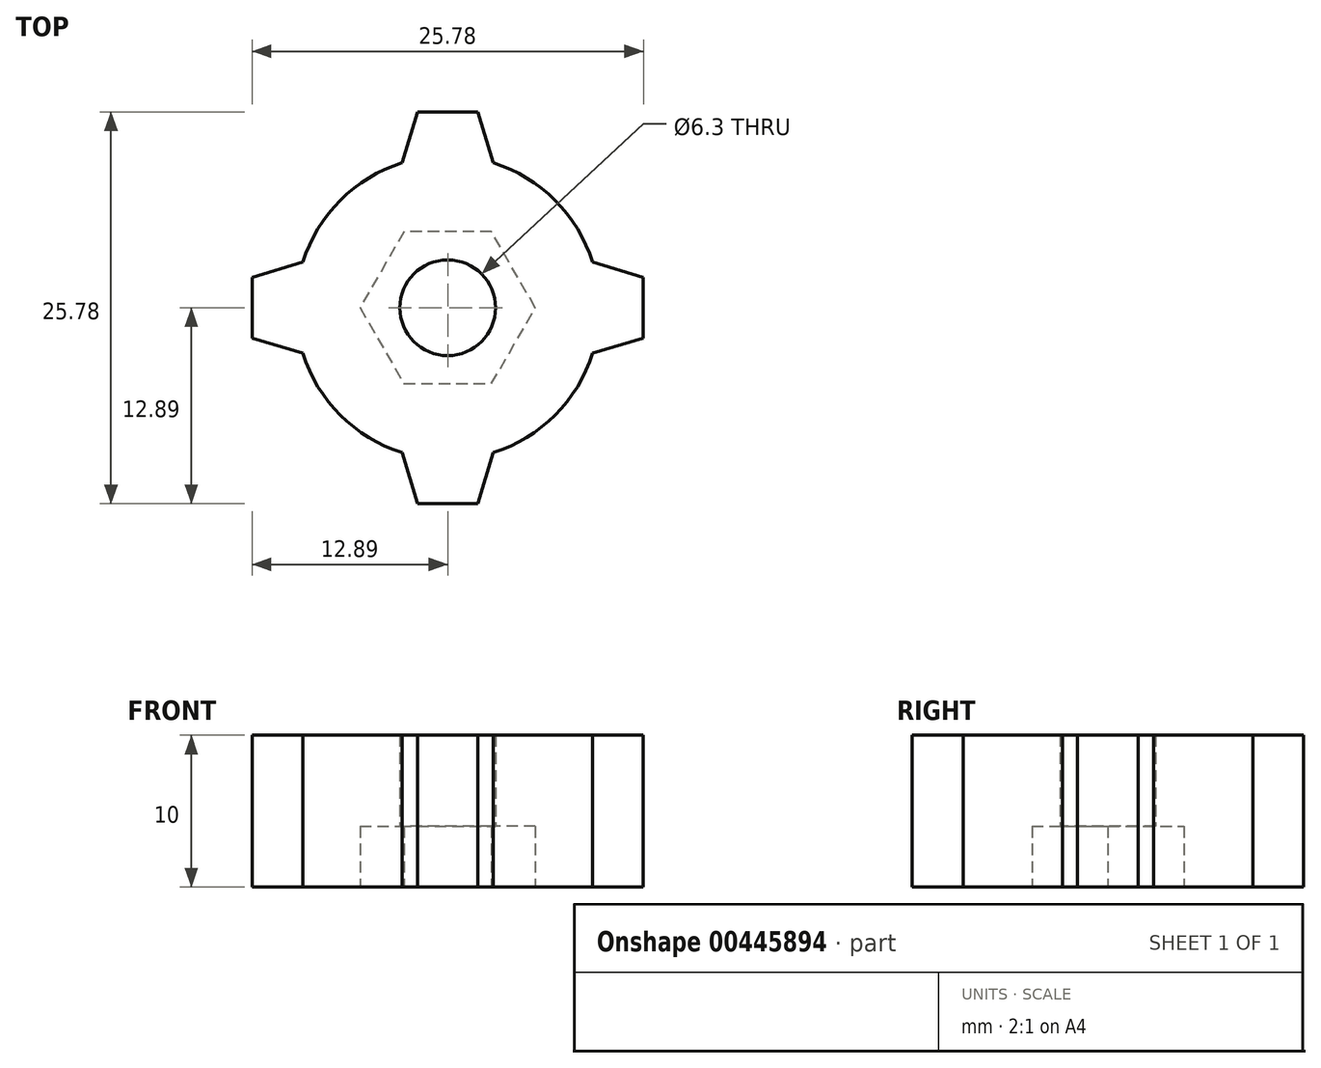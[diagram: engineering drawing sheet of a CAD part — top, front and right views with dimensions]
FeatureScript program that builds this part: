
annotation { "Feature Type Name" : "Feature", "Feature Type Description" : "" }
export const myFeature = defineFeature(function(context is Context, id is Id, definition is map)
    precondition{}
    {
        {
            var Q0;
            Q0=qCreatedBy(makeId("Top.planeOp"),FACE);
            var sketch = newSketch(context, id + "F0", { "sketchPlane" : qUnion([Q0])});
            skCircle(sketch, "E0", {"center": v(0, 0) * mm, "radius": 10 * mm});
            skPoint(sketch, "E1", {"position": v(0, -10) * mm});
            skLineSegment(sketch, "E2", {"start": v(-3, -9.54) * mm, "end": v(-2, -12.89) * mm});
            skLineSegment(sketch, "E3", {"start": v(-2, -12.89) * mm, "end": v(0, -12.89) * mm});
            skLineSegment(sketch, "E4", {"start": v(0, -12.89) * mm, "end": v(0, -10) * mm, "construction": true});
            skLineSegment(sketch, "E5.MirrorCS", {"start": v(2, -12.89) * mm, "end": v(0, -12.89) * mm});
            skLineSegment(sketch, "E6.MirrorCS", {"start": v(3, -9.54) * mm, "end": v(2, -12.89) * mm});
            skSolve(sketch);
        }
        {
            var Q0;
            Q0=makeQuery(id+"F0.imprint","IMPRINT",FACE,{"disambiguationData":[TD([[makeQuery(id+"F0.imprint","IMPRINT",EDGE,{"derivedFrom":sQuery(id+"F0.wireOp",EDGE,"E0")}),1.0]])]});
            extrude(context, id + "F1", {"entities" : qUnion([Q0]), "depth" : 10 * mm});
        }
        {
            var Q0;
            Q0=makeQuery(id+"F1.opExtrude","CAP_FACE",FACE,{"disambiguationData":[OSD([sQuery(id+"F0.wireOp",EDGE,"E0")])],"isStart":true});
            var sketch = newSketch(context, id + "F2", { "sketchPlane" : qUnion([Q0])});
            skCircle(sketch, "E7.cCircle", {"center": v(0, 0) * mm, "radius": 5 * mm, "construction": true});
            skLineSegment(sketch, "E7.0", {"start": v(2.89, -5) * mm, "end": v(-2.89, -5) * mm});
            skLineSegment(sketch, "E7.1", {"start": v(-2.89, -5) * mm, "end": v(-5.77, 0) * mm});
            skLineSegment(sketch, "E7.2", {"start": v(-5.77, 0) * mm, "end": v(-2.89, 5) * mm});
            skLineSegment(sketch, "E7.3", {"start": v(-2.89, 5) * mm, "end": v(2.89, 5) * mm});
            skLineSegment(sketch, "E7.4", {"start": v(2.89, 5) * mm, "end": v(5.77, 0) * mm});
            skLineSegment(sketch, "E7.5", {"start": v(5.77, 0) * mm, "end": v(2.89, -5) * mm});
            skPoint(sketch, "E7.0.midPoint", {"position": v(0, -5) * mm});
            skSolve(sketch);
        }
        {
            var Q0;
            Q0=makeQuery(id+"F2.imprint","IMPRINT",FACE,{"disambiguationData":[TD([[makeQuery(id+"F2.imprint","IMPRINT",EDGE,{"derivedFrom":sQuery(id+"F2.wireOp",EDGE,"E7.0")}),-1.0]])]});
            extrude(context, id + "F3", {"entities" : qUnion([Q0]), "operationType" : NewBodyOperationType.REMOVE, "oppositeDirection" : true, "depth" : 4 * mm});
        }
        {
            var Q0;
            Q0=sQuery(id+"F2.wireOp",VERTEX,"E7.cCircle.center");
            var Q1;
            Q1=makeQuery(id+"F1.opExtrude","SWEPT_BODY",BODY,{"disambiguationData":[OSD([sQuery(id+"F0.wireOp",EDGE,"E0")])]});
            hole(context, id + "F4", {"style" : HoleStyle.SIMPLE, "endStyle" : HoleEndStyle.THROUGH, "standardTappedOrClearance" : lookupTablePath({ "standard" : "ISO", "fit" : "Close", "size" : "M6", "type" : "Clearance" }), "standardBlindInLast" : lookupTablePath({ "fit" : "Close", "standard" : "ISO", "size" : "M6", "type" : "Clearance" }), "holeDiameter" : 6.3 * mm, "isTappedThrough" : true, "tappedDepth" : 12 * mm, "tapClearance" : 3, "locations" : qUnion([Q0]), "scope" : qUnion([Q1])});
        }
        {
            var Q0;
            {var subQ0=sQuery(id+"F0.wireOp",EDGE,"E2");Q0=makeQuery(id+"F0.imprint","IMPRINT",FACE,{"disambiguationData":[TD([[makeQuery(id+"F0.imprint","IMPRINT",EDGE,{"derivedFrom":subQ0}),1.0]])]});}
            var Q1;
            Q1=makeQuery(id+"F1.opExtrude","CAP_FACE",FACE,{"disambiguationData":[OSD([sQuery(id+"F0.wireOp",EDGE,"E0")])],"isStart":false});
            extrude(context, id + "F5", {"entities" : qUnion([Q0]), "endBound" : BoundingType.UP_TO_SURFACE, "endBoundEntityFace" : qUnion([Q1]), "depth" : 25 * mm});
        }
        {
            var Q0;
            Q0=qCreatedBy(makeId("Front.planeOp"),FACE);
            var sketch = newSketch(context, id + "F6", { "sketchPlane" : qUnion([Q0])});
            skLineSegment(sketch, "E8", {"start": v(0, 0) * mm, "end": v(0, -24.05) * mm});
            skSolve(sketch);
        }
        {
            var Q0;
            Q0=makeQuery(id+"F5.opExtrude","SWEPT_BODY",BODY,{"disambiguationData":[OSD([sQuery(id+"F0.wireOp",EDGE,"E0"),sQuery(id+"F0.wireOp",EDGE,"E2"),sQuery(id+"F0.wireOp",EDGE,"E3"),sQuery(id+"F0.wireOp",EDGE,"E5.MirrorCS"),sQuery(id+"F0.wireOp",EDGE,"E6.MirrorCS")])]});
            var Q1;
            Q1=sQuery(id+"F6.wireOp",EDGE,"E8");
            circularPattern(context, id + "F7", {"operationType" : NewBodyOperationType.ADD, "entities" : qUnion([Q0]), "axis" : qUnion([Q1]), "angle" : 360 * degree, "instanceCount" : 4, "equalSpace" : true});
        }
    });
